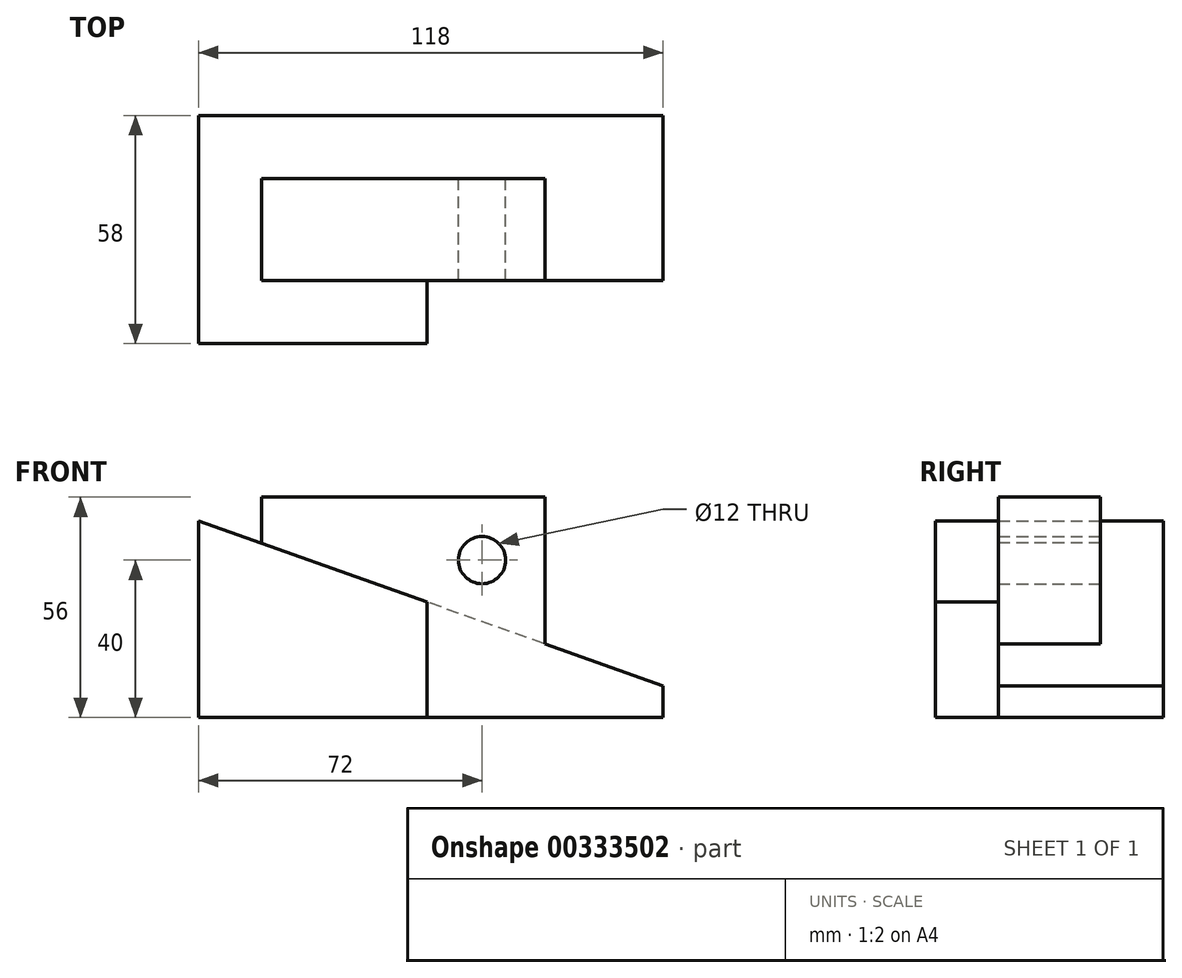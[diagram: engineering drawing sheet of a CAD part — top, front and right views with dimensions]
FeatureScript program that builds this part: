
annotation { "Feature Type Name" : "Feature", "Feature Type Description" : "" }
export const myFeature = defineFeature(function(context is Context, id is Id, definition is map)
    precondition{}
    {
        {
            var Q0;
            Q0=qCreatedBy(makeId("Front.planeOp"),FACE);
            var sketch = newSketch(context, id + "F0", { "sketchPlane" : qUnion([Q0])});
            skLineSegment(sketch, "E0", {"start": v(0, 50) * mm, "end": v(0, 0) * mm});
            skLineSegment(sketch, "E1", {"start": v(0, 0) * mm, "end": v(118, 0) * mm});
            skLineSegment(sketch, "E2", {"start": v(118, 0) * mm, "end": v(118, 8) * mm});
            skLineSegment(sketch, "E3", {"start": v(118, 8) * mm, "end": v(0, 50) * mm});
            skSolve(sketch);
        }
        {
            var Q0;
            Q0=makeQuery(id+"F0.imprint","IMPRINT",FACE,{"disambiguationData":[TD([[makeQuery(id+"F0.imprint","IMPRINT",EDGE,{"derivedFrom":sQuery(id+"F0.wireOp",EDGE,"E0")}),1.0]])]});
            extrude(context, id + "F1", {"entities" : qUnion([Q0]), "depth" : 58 * mm});
        }
        {
            var Q0;
            Q0=makeQuery(id+"F1.opExtrude","CAP_FACE",FACE,{"disambiguationData":[OSD([sQuery(id+"F0.wireOp",EDGE,"E0"),sQuery(id+"F0.wireOp",EDGE,"E1"),sQuery(id+"F0.wireOp",EDGE,"E2"),sQuery(id+"F0.wireOp",EDGE,"E3")])],"isStart":false});
            var sketch = newSketch(context, id + "F2", { "sketchPlane" : qUnion([Q0])});
            skLineSegment(sketch, "E4", {"start": v(118, 8) * mm, "end": v(118, 0) * mm});
            skLineSegment(sketch, "E5", {"start": v(118, 0) * mm, "end": v(58, 0) * mm});
            skLineSegment(sketch, "E6", {"start": v(58, 0) * mm, "end": v(58, 29.36) * mm});
            skLineSegment(sketch, "E7", {"start": v(58, 29.36) * mm, "end": v(118, 8) * mm});
            skSolve(sketch);
        }
        {
            var Q0;
            Q0=makeQuery(id+"F2.imprint","IMPRINT",FACE,{"disambiguationData":[TD([[makeQuery(id+"F2.imprint","IMPRINT",EDGE,{"derivedFrom":sQuery(id+"F2.wireOp",EDGE,"E4")}),1.0]])]});
            extrude(context, id + "F3", {"entities" : qUnion([Q0]), "operationType" : NewBodyOperationType.REMOVE, "oppositeDirection" : true, "depth" : 16 * mm});
        }
        {
            var Q0;
            Q0=makeQuery(id+"F1.opExtrude","SWEPT_FACE",FACE,{"disambiguationData":[OSD([sQuery(id+"F0.wireOp",EDGE,"E1")])]});
            var sketch = newSketch(context, id + "F4", { "sketchPlane" : qUnion([Q0])});
            skLineSegment(sketch, "E8", {"start": v(88, 42) * mm, "end": v(88, 16) * mm});
            skLineSegment(sketch, "E9", {"start": v(88, 16) * mm, "end": v(16, 16) * mm});
            skLineSegment(sketch, "E10", {"start": v(16, 16) * mm, "end": v(16, 42) * mm});
            skLineSegment(sketch, "E11", {"start": v(16, 42) * mm, "end": v(88, 42) * mm});
            skSolve(sketch);
        }
        {
            var Q0;
            {var subQ4=sQuery(id+"F4.wireOp",EDGE,"E8");Q0=makeQuery(id+"F4.imprint","IMPRINT",FACE,{"disambiguationData":[TD([[makeQuery(id+"F4.imprint","IMPRINT",EDGE,{"derivedFrom":subQ4}),-1.0]])]});}
            extrude(context, id + "F5", {"entities" : qUnion([Q0]), "operationType" : NewBodyOperationType.ADD, "oppositeDirection" : true, "depth" : 56 * mm});
        }
        {
            var Q0;
            Q0=makeQuery(id+"F5.opExtrude","SWEPT_FACE",FACE,{"disambiguationData":[OSD([sQuery(id+"F4.wireOp",EDGE,"E9")])]});
            var sketch = newSketch(context, id + "F6", { "sketchPlane" : qUnion([Q0])});
            skCircle(sketch, "E12", {"center": v(-72, 40) * mm, "radius": 6 * mm});
            skSolve(sketch);
        }
        {
            var Q0;
            Q0=makeQuery(id+"F6.imprint","IMPRINT",FACE,{"disambiguationData":[TD([[makeQuery(id+"F6.imprint","IMPRINT",EDGE,{"derivedFrom":sQuery(id+"F6.wireOp",EDGE,"E12")}),1.0]])]});
            extrude(context, id + "F7", {"entities" : qUnion([Q0]), "operationType" : NewBodyOperationType.REMOVE, "endBound" : BoundingType.THROUGH_ALL, "oppositeDirection" : true, "depth" : 25 * mm});
        }
    });
